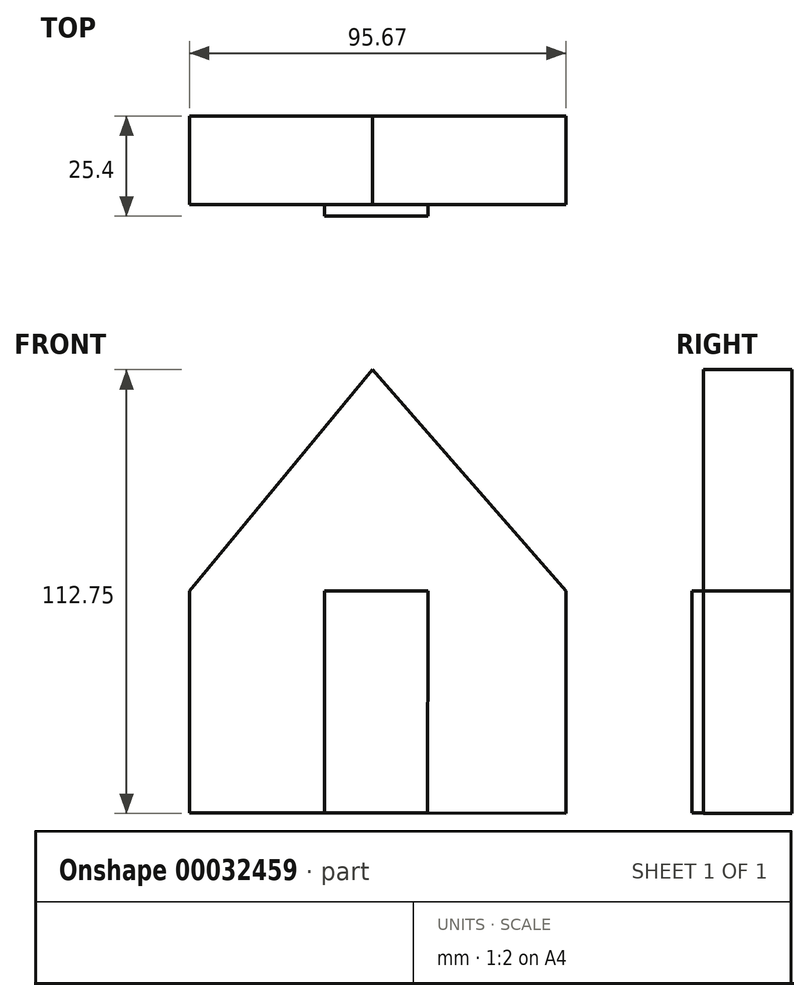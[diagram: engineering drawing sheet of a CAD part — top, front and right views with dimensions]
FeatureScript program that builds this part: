
annotation { "Feature Type Name" : "Feature", "Feature Type Description" : "" }
export const myFeature = defineFeature(function(context is Context, id is Id, definition is map)
    precondition{}
    {
        {
            var Q0;
            Q0=qCreatedBy(makeId("Front.planeOp"),FACE);
            var sketch = newSketch(context, id + "F0", { "sketchPlane" : qUnion([Q0])});
            skLineSegment(sketch, "E0", {"start": v(0, 56.28) * mm, "end": v(-46.5, 0) * mm});
            skLineSegment(sketch, "E1", {"start": v(0, 56.28) * mm, "end": v(49.16, 0) * mm});
            skLineSegment(sketch, "E2", {"start": v(-46.5, 0) * mm, "end": v(-46.5, -56.28) * mm});
            skLineSegment(sketch, "E3", {"start": v(49.16, 0) * mm, "end": v(49.16, -56.47) * mm});
            skLineSegment(sketch, "E4", {"start": v(-46.5, -56.28) * mm, "end": v(49.16, -56.47) * mm});
            skSolve(sketch);
        }
        {
            var Q0;
            Q0=makeQuery(id+"F0.imprint","IMPRINT",FACE,{"disambiguationData":[TD([[makeQuery(id+"F0.imprint","IMPRINT",EDGE,{"derivedFrom":sQuery(id+"F0.wireOp",EDGE,"E0")}),1.0]])]});
            extrude(context, id + "F1", {"entities" : qUnion([Q0]), "depth" : 25.4 * mm});
        }
        {
            var Q0;
            Q0=makeQuery(id+"F1.opExtrude","CAP_FACE",FACE,{"disambiguationData":[OSD([sQuery(id+"F0.wireOp",EDGE,"E0"),sQuery(id+"F0.wireOp",EDGE,"E1"),sQuery(id+"F0.wireOp",EDGE,"E2"),sQuery(id+"F0.wireOp",EDGE,"E3"),sQuery(id+"F0.wireOp",EDGE,"E4")])],"isStart":false});
            var sketch = newSketch(context, id + "F2", { "sketchPlane" : qUnion([Q0])});
            skLineSegment(sketch, "E5", {"start": v(13.99, -56.4) * mm, "end": v(14.1, 0) * mm});
            skLineSegment(sketch, "E6", {"start": v(14.1, 0) * mm, "end": v(-12.16, 0.05) * mm});
            skLineSegment(sketch, "E7", {"start": v(-12.16, 0.05) * mm, "end": v(-12.16, -56.35) * mm});
            skSolve(sketch);
        }
        {
            var Q0;
            {var subQ1=sQuery(id+"F2.wireOp",EDGE,"E5");Q0=makeQuery(id+"F2.imprint","IMPRINT",FACE,{"disambiguationData":[TD([[makeQuery(id+"F2.imprint","IMPRINT",EDGE,{"derivedFrom":subQ1}),-1.0]])]});}
            extrude(context, id + "F3", {"entities" : qUnion([Q0]), "operationType" : NewBodyOperationType.REMOVE, "oppositeDirection" : true, "depth" : 2.9 * mm});
        }
    });
